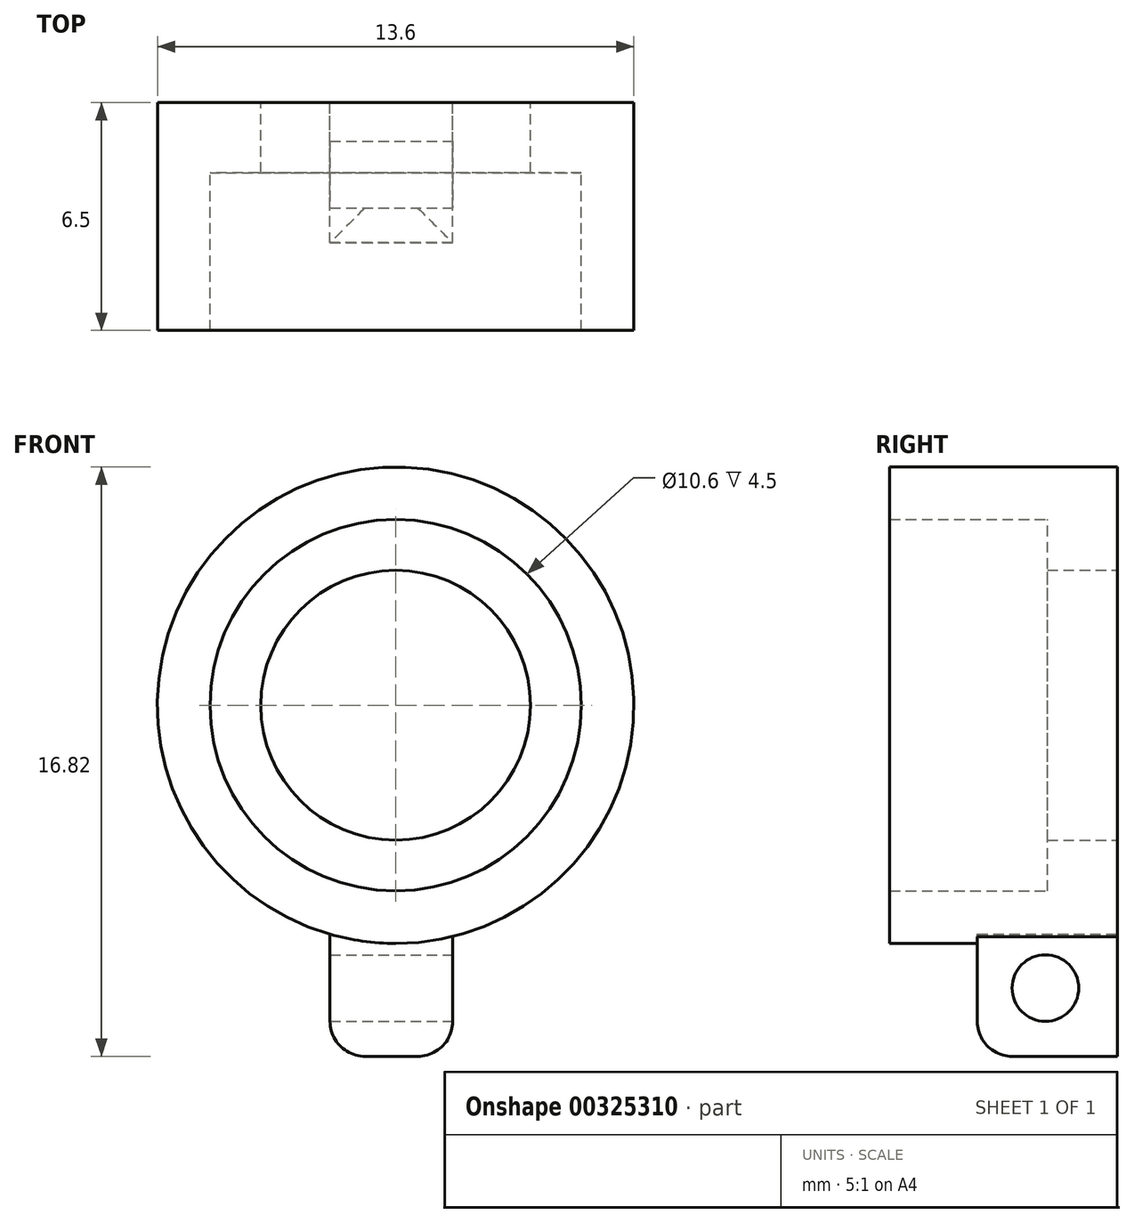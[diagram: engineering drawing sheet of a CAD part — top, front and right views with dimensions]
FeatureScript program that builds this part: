
annotation { "Feature Type Name" : "Feature", "Feature Type Description" : "" }
export const myFeature = defineFeature(function(context is Context, id is Id, definition is map)
    precondition{}
    {
        {
            var Q0;
            Q0=qCreatedBy(makeId("Front.planeOp"),FACE);
            var sketch = newSketch(context, id + "F0", { "sketchPlane" : qUnion([Q0])});
            skCircle(sketch, "E0", {"center": v(0, 0) * mm, "radius": 3.85 * mm});
            skCircle(sketch, "E1", {"center": v(0, 0) * mm, "radius": 5.3 * mm});
            skArc(sketch, "E2", {"start": v(6.8, 0) * mm, "mid": v(0, 6.8) * mm, "end": v(-6.8, 0) * mm});
            skLineSegment(sketch, "E3.left", {"start": v(-6.8, 0) * mm, "end": v(-6.8, 0) * mm});
            skLineSegment(sketch, "E3.right", {"start": v(6.8, 0) * mm, "end": v(6.8, 0) * mm});
            skArc(sketch, "E4.trimOffspring", {"start": v(-6.8, 0) * mm, "mid": v(0, -6.8) * mm, "end": v(6.8, 0) * mm});
            skLineSegment(sketch, "E5.bottom", {"start": v(1.63, -10.02) * mm, "end": v(-1.87, -10.02) * mm});
            skLineSegment(sketch, "E5.left", {"start": v(1.63, -10.02) * mm, "end": v(1.63, -6.6) * mm});
            skLineSegment(sketch, "E5.right", {"start": v(-1.87, -10.02) * mm, "end": v(-1.87, -6.54) * mm});
            skPoint(sketch, "E5.middle", {"position": v(-0.12, -7.52) * mm});
            skPoint(sketch, "E5.top.end.orphan", {"position": v(-1.87, -5.02) * mm});
            skPoint(sketch, "E6.orphan", {"position": v(1.63, -5.02) * mm});
            skSolve(sketch);
        }
        {
            var Q0;
            Q0=makeQuery(id+"F0.imprint","IMPRINT",FACE,{"disambiguationData":[TD([[makeQuery(id+"F0.imprint","IMPRINT",EDGE,{"derivedFrom":sQuery(id+"F0.wireOp",EDGE,"E0")}),-1.0]])]});
            extrude(context, id + "F1", {"entities" : qUnion([Q0]), "depth" : 2 * mm});
        }
        {
            var Q0;
            Q0=makeQuery(id+"F0.imprint","IMPRINT",FACE,{"disambiguationData":[TD([[makeQuery(id+"F0.imprint","IMPRINT",EDGE,{"derivedFrom":sQuery(id+"F0.wireOp",EDGE,"E1")}),-1.0]])]});
            extrude(context, id + "F2", {"entities" : qUnion([Q0]), "operationType" : NewBodyOperationType.ADD, "depth" : 6.5 * mm});
        }
        {
            var Q0;
            Q0=makeQuery(id+"F0.imprint","IMPRINT",FACE,{"disambiguationData":[TD([[makeQuery(id+"F0.imprint","IMPRINT",EDGE,{"derivedFrom":sQuery(id+"F0.wireOp",EDGE,"E5.bottom")}),-1.0]])]});
            extrude(context, id + "F3", {"entities" : qUnion([Q0]), "operationType" : NewBodyOperationType.ADD, "depth" : 4 * mm});
        }
        {
            var Q0;
            Q0=makeQuery(id+"F3.opExtrude","SWEPT_FACE",FACE,{"disambiguationData":[OSD([sQuery(id+"F0.wireOp",EDGE,"E5.left")])]});
            var sketch = newSketch(context, id + "F4", { "sketchPlane" : qUnion([Q0])});
            skCircle(sketch, "E7", {"center": v(-2.06, -8.07) * mm, "radius": 0.95 * mm});
            skSolve(sketch);
        }
        {
            var Q0;
            Q0=makeQuery(id+"F4.imprint","IMPRINT",FACE,{"disambiguationData":[TD([[makeQuery(id+"F4.imprint","IMPRINT",EDGE,{"derivedFrom":sQuery(id+"F4.wireOp",EDGE,"E7")}),1.0]])]});
            var Q1;
            Q1=sQuery(id+"F4.wireOp",EDGE,"E7");
            extrude(context, id + "F5", {"entities" : qUnion([Q0]), "operationType" : NewBodyOperationType.REMOVE, "surfaceEntities" : qUnion([Q1]), "oppositeDirection" : true, "depth" : 25.4 * mm});
        }
        {
            var Q0;
            Q0=makeQuery(id+"F3.opExtrude","SWEPT_EDGE",EDGE,{"disambiguationData":[OSD([sQuery(id+"F0.wireOp",EDGE,"E5.bottom"),sQuery(id+"F0.wireOp",EDGE,"E5.left")])]});
            var Q1;
            Q1=makeQuery(id+"F3.opExtrude","SWEPT_EDGE",EDGE,{"disambiguationData":[OSD([sQuery(id+"F0.wireOp",EDGE,"E5.bottom"),sQuery(id+"F0.wireOp",EDGE,"E5.right")])]});
            var Q2;
            Q2=makeQuery(id+"F3.opExtrude","CAP_EDGE",EDGE,{"disambiguationData":[OSD([sQuery(id+"F0.wireOp",EDGE,"E5.bottom")])],"isStart":false});
            fillet(context, id + "F6", {"entities" : qUnion([Q0, Q1, Q2]), "radius" : 1 * mm, "tangentPropagation" : true, "allowEdgeOverflow" : false});
        }
    });
